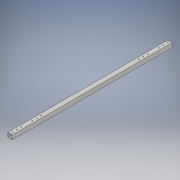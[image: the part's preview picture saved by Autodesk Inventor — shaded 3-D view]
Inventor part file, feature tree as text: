
AUTODESK INVENTOR PART (.ipt)
format: ipt  version: 2018 (Build 220112000, 112)  size: 139,776 bytes
history: native  units: in
note: dims shown in document units (in); Inventor stores cm internally (conversion verified against a paired STEP export)
features: extrude x2, sketch x2
ambient origin geometry x8: Origin, YZ Plane, XZ Plane, XY Plane, X Axis, Y Axis, Z Axis, Center Point
bodies: Solid1 (feature_tree)
feature tree (4):
  extrude  "Extrusion1"  Depth=1.0in
  extrude  "Extrusion2"  Depth=36.0in TaperAngle=0.0deg
  sketch  "Sketch1"  dims[d0=1.0in d1=1.0in]
  sketch  "Sketch2"  dims[d2=0.125in d3=36.0in d4=0.0in d5=0.5in d6=1.0in d7=1.0in d8=6.0in d9=1.0in d10=2.0in d11=0.2031in d12=36.0in d13=0.0in]
